FCSTD DOCUMENT  (FreeCAD 0.14R3702 (Git))
Label: TopInnerCornerMotorSupport
License: CC-BY 3.0
LicenseURL: http://creativecommons.org/licenses/by/3.0/
objects: Sketcher::SketchObject×1
note: 1 computed .brp shape members not serialized (recipe doc carries the construction recipe); baked Part::Feature solids carry a one-line shape summary decoded from their .brp

FEATURE [Sketcher::SketchObject] Sketch
  sketch-geometry (17):
    g0: LineSegment StartX=0 StartY=20 StartZ=0 EndX=0 EndY=40 EndZ=0
    g1: LineSegment StartX=0 StartY=39.7546 StartZ=0 EndX=85 EndY=39.7546 EndZ=0
    g2: LineSegment StartX=85 StartY=39.7546 StartZ=0 EndX=85 EndY=19.7546 EndZ=0
    g3: LineSegment StartX=85 StartY=19.7546 StartZ=0 EndX=105 EndY=19.7546 EndZ=0
    g4: LineSegment StartX=105 StartY=19.7546 StartZ=0 EndX=105 EndY=-20.2454 EndZ=0
    g5: LineSegment StartX=85 StartY=0 StartZ=0 EndX=85 EndY=-20 EndZ=0
    g6: LineSegment StartX=85 StartY=-20.2454 StartZ=0 EndX=105 EndY=-20.2454 EndZ=0
    g7: LineSegment StartX=85 StartY=0 StartZ=0 EndX=65 EndY=20 EndZ=0
    g8: LineSegment StartX=0 StartY=20 StartZ=0 EndX=65 EndY=20 EndZ=0
    g9: LineSegment [constr] StartX=85 StartY=30 StartZ=0 EndX=67 EndY=30 EndZ=0
    g10: Circle CenterX=67 CenterY=30 CenterZ=0 NormalX=0 NormalY=0 NormalZ=1 Radius=2.01
    g11: LineSegment [constr] StartX=67 StartY=30 StartZ=0 EndX=12 EndY=30 EndZ=0
    g12: Circle CenterX=12 CenterY=30 CenterZ=0 NormalX=0 NormalY=0 NormalZ=1 Radius=2.01
    g13: LineSegment [constr] StartX=95 StartY=19.7546 StartZ=0 EndX=95 EndY=9.75461 EndZ=0
    g14: Circle CenterX=95 CenterY=9.75461 CenterZ=0 NormalX=0 NormalY=0 NormalZ=1 Radius=2.01
    g15: LineSegment [constr] StartX=95 StartY=9.75461 StartZ=0 EndX=95 EndY=-5.24539 EndZ=0
    g16: Circle CenterX=95 CenterY=-5.24539 CenterZ=0 NormalX=0 NormalY=0 NormalZ=1 Radius=2.01
  constraints (45):
    c: PointOnObject(g0,g-2)
    c: Vertical(g0)
    c: PointOnObject(g1,g0)
    c: Horizontal(g1)
    c: DistanceX(g1) = 85
    c: Coincident(g2,g1)
    c: Vertical(g2)
    c: Coincident(g3,g2)
    c: Horizontal(g3)
    c: Coincident(g4,g3)
    c: Vertical(g4)
    c: PointOnObject(g5,g-1)
    c: Vertical(g5)
    c: Coincident(g6,g4)
    c: Horizontal(g6)
    c: DistanceY(g4) = -40
    c: DistanceY(g2) = -20
    c: Equal(g2,g3)
    c: DistanceY(g5) = -20
    c: Coincident(g8,g0)
    c: Coincident(g8,g7)
    c: Horizontal(g8)
    c: DistanceX(g8) = 65
    c: Equal(g0,g2)
    c: Equal(g3,g6)
    c: PointOnObject(g9,g2)
    c: Horizontal(g9)
    c: DistanceX(g9) = -18
    c: Coincident(g10,g9)
    c: Radius(g10) = 2.01
    c: Coincident(g11,g9)
    c: Horizontal(g11)
    c: DistanceX(g11) = -55
    c: Coincident(g12,g11)
    c: Equal(g12,g10)
    c: PointOnObject(g13,g3)
    c: Vertical(g13)
    c: DistanceY(g13) = -10
    c: Coincident(g14,g13)
    c: Coincident(g15,g13)
    c: Vertical(g15)
    c: DistanceY(g15) = -15
    c: Coincident(g16,g15)
    c: Equal(g14,g10)
    c: Equal(g14,g16)
